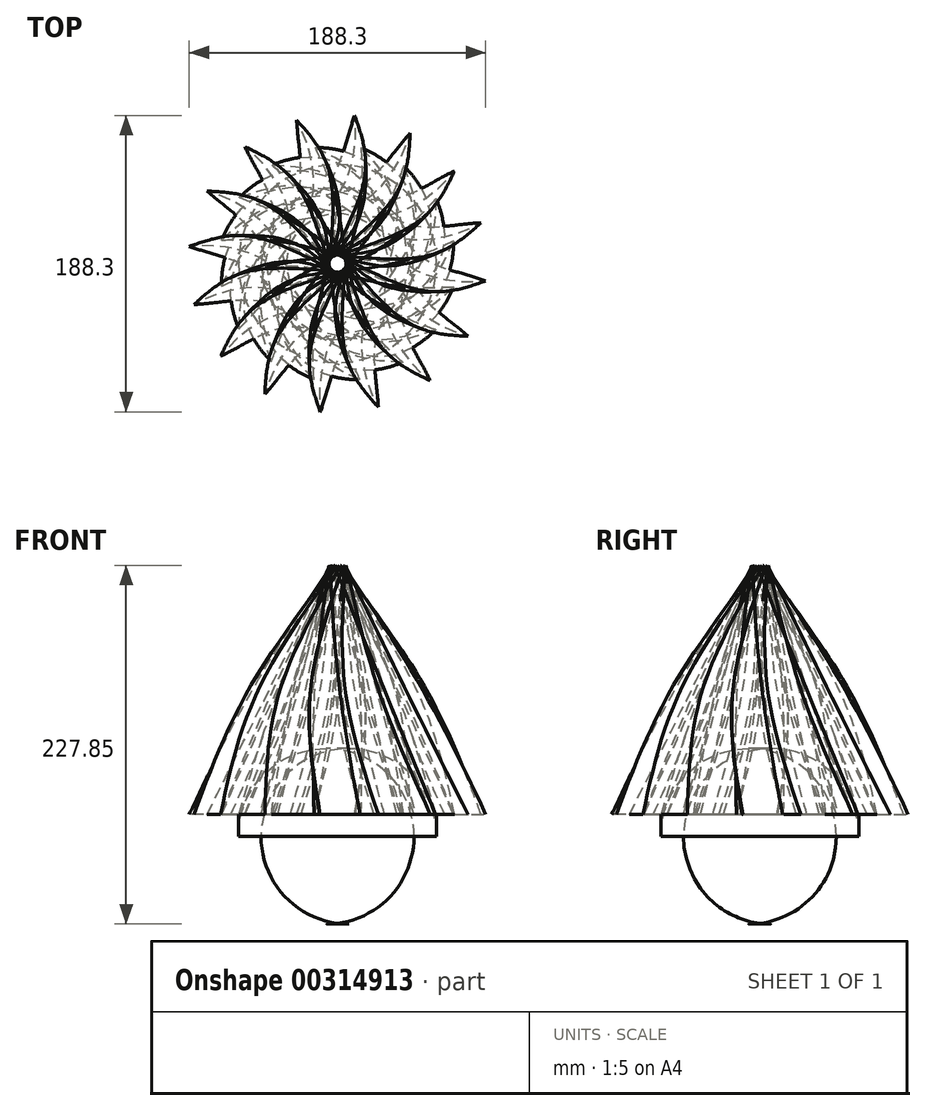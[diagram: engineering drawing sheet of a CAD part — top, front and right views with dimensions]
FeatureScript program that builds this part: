
annotation { "Feature Type Name" : "Feature", "Feature Type Description" : "" }
export const myFeature = defineFeature(function(context is Context, id is Id, definition is map)
    precondition{}
    {
        {
            var Q0;
            Q0=qCreatedBy(makeId("Top.planeOp"),FACE);
            var sketch = newSketch(context, id + "F0", { "sketchPlane" : qUnion([Q0])});
            skFitSpline(sketch, "E0", {"points": [v(-73.57, 14.97) * mm, v(-39.74, 36.82) * mm, v(0, 32.57) * mm, v(37.25, 32.1) * mm, v(74.3, 58.83) * mm], "startDerivative": vector(122.11, 115.06) * mm, "endDerivative": vector(107, 134.25) * mm});
            skFitSpline(sketch, "E1", {"points": [v(-73.57, 14.97) * mm, v(-46.63, 44.74) * mm, v(0, 45.83) * mm, v(35.17, 40.8) * mm, v(74.3, 58.83) * mm], "startDerivative": vector(65.78, 162.55) * mm, "endDerivative": vector(139, 63.16) * mm});
            skPoint(sketch, "E2", {"position": v(0, 40.44) * mm});
            skSolve(sketch);
        }
        {
            var Q0;
            Q0=qCreatedBy(makeId("Top.planeOp"),FACE);
            cPlane(context, id + "F1", {"entities" : qUnion([Q0]), "cplaneType" : CPlaneType.OFFSET, "offset" : 158.06 * mm, "width" : 152.4 * mm, "height" : 152.4 * mm});
        }
        {
            var Q0;
            Q0=qCreatedBy(id+"F1.planeOp",FACE);
            var sketch = newSketch(context, id + "F2", { "sketchPlane" : qUnion([Q0])});
            skPoint(sketch, "E3", {"position": v(0, 5.37) * mm});
            skSolve(sketch);
        }
        {
            var Q0;
            Q0=qCreatedBy(makeId("Top.planeOp"),FACE);
            cPlane(context, id + "F3", {"entities" : qUnion([Q0]), "cplaneType" : CPlaneType.OFFSET, "offset" : 78.05 * mm, "width" : 152.4 * mm, "height" : 152.4 * mm});
        }
        {
            var Q0;
            Q0=qCreatedBy(id+"F3.planeOp",FACE);
            var sketch = newSketch(context, id + "F4", { "sketchPlane" : qUnion([Q0])});
            skFitSpline(sketch, "E4", {"points": [v(-38.66, 14.42) * mm, v(-17.6, 24.78) * mm, v(0, 22.21) * mm, v(27.52, 15.93) * mm, v(50.76, 26.45) * mm], "startDerivative": vector(86.99, 54.78) * mm, "endDerivative": vector(84.16, 56.87) * mm});
            skFitSpline(sketch, "E5", {"points": [v(-38.66, 14.42) * mm, v(-17.6, 20.2) * mm, v(0, 17.3) * mm, v(27.52, 11.19) * mm, v(50.76, 26.45) * mm], "startDerivative": vector(91.79, 32.02) * mm, "endDerivative": vector(78.59, 85.88) * mm});
            skSolve(sketch);
        }
        {
            var Q0;
            Q0=makeQuery(id+"F0.imprint","IMPRINT",FACE,{"disambiguationData":[TD([[makeQuery(id+"F0.imprint","IMPRINT",EDGE,{"derivedFrom":sQuery(id+"F0.wireOp",EDGE,"E0")}),1.0]])]});
            var Q1;
            Q1=makeQuery(id+"F4.imprint","IMPRINT",FACE,{"disambiguationData":[TD([[makeQuery(id+"F4.imprint","IMPRINT",EDGE,{"derivedFrom":sQuery(id+"F4.wireOp",EDGE,"E4")}),-1.0]])]});
            var Q2;
            Q2=sQuery(id+"F2.wireOp",VERTEX,"E3");
            loft(context, id + "F5", {"sheetProfilesArray" : [{ "sheetProfileEntities" : qUnion([Q0]) }, { "sheetProfileEntities" : qUnion([Q1]) }, { "sheetProfileEntities" : qUnion([Q2]) }]});
        }
        {
            var Q0;
            Q0=qCreatedBy(makeId("Front.planeOp"),FACE);
            var sketch = newSketch(context, id + "F6", { "sketchPlane" : qUnion([Q0])});
            skLineSegment(sketch, "E6", {"start": v(0, 0) * mm, "end": v(0, 165.82) * mm});
            skSolve(sketch);
        }
        {
            var Q0;
            Q0=makeQuery(id+"F5.opLoft","SWEPT_BODY",BODY,{"disambiguationData":[OSD([makeQuery(id+"F0.imprint","IMPRINT",FACE,{"disambiguationData":[TD([[makeQuery(id+"F0.imprint","IMPRINT",EDGE,{"derivedFrom":sQuery(id+"F0.wireOp",EDGE,"E0")}),1.0]])]}),sQuery(id+"F2.wireOp",VERTEX,"E3"),sQuery(id+"F4.wireOp",EDGE,"E4")])]});
            var Q1;
            Q1=sQuery(id+"F6.wireOp",EDGE,"E6");
            circularPattern(context, id + "F7", {"entities" : qUnion([Q0]), "axis" : qUnion([Q1]), "angle" : 360 * degree, "instanceCount" : 16, "equalSpace" : true});
        }
        {
            var Q0;
            Q0=qCreatedBy(makeId("Top.planeOp"),FACE);
            var sketch = newSketch(context, id + "F8", { "sketchPlane" : qUnion([Q0])});
            skCircle(sketch, "E7", {"center": v(0, 0) * mm, "radius": 62.94 * mm});
            skSolve(sketch);
        }
        {
            var Q0;
            Q0 = qSketchRegion(id + "F8", true);
            extrude(context, id + "F9", {"entities" : qUnion([Q0]), "oppositeDirection" : true, "depth" : 69.8 * mm});
        }
        {
            var Q0;
            Q0=makeQuery(id+"F9.opExtrude","CAP_EDGE",EDGE,{"disambiguationData":[OSD([sQuery(id+"F8.wireOp",EDGE,"E7")])],"isStart":false});
            fillet(context, id + "F10", {"entities" : qUnion([Q0]), "radius" : 55.75 * mm, "tangentPropagation" : true, "allowEdgeOverflow" : false});
        }
    });
